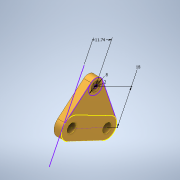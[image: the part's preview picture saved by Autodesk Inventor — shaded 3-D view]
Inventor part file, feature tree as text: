
AUTODESK INVENTOR PART (.ipt)
format: ipt  version: 2020 (Build 240168000, 168)  size: 154,112 bytes
history: native  units: in
note: dims shown in document units (in); Inventor stores cm internally (conversion verified against a paired STEP export)
features: extrude x3, sketch x3, projected_geometry x1
ambient origin geometry x8: Origin, YZ Plane, XZ Plane, XY Plane, X Axis, Y Axis, Z Axis, Center Point
bodies: Solid1 (feature_tree)
feature tree (7):
  extrude  "Extrusion1"  Depth=0.4523in
  extrude  "Extrusion2"  Depth=0.2118in
  extrude  "Extrusion3"  Depth=0.1575in TaperAngle=0.0deg
  sketch  "Sketch1"  dims[d0=0.2008in d1=0.2008in d3=0.4523in]
  sketch  "Sketch2"  dims[d4=0.2118in d5=0.8586in]
  projected_geometry  "Projected Loop1"
  sketch  "Sketch3"  dims[d6=0.8656in d7=0.1575in d8=0.0in d11=0.0787in d12=0.315in d13=0.1575in d14=0.0in d15=0.1969in d16=0.0787in d17=0.0in d20=0.7087in d21=0.4622in]
